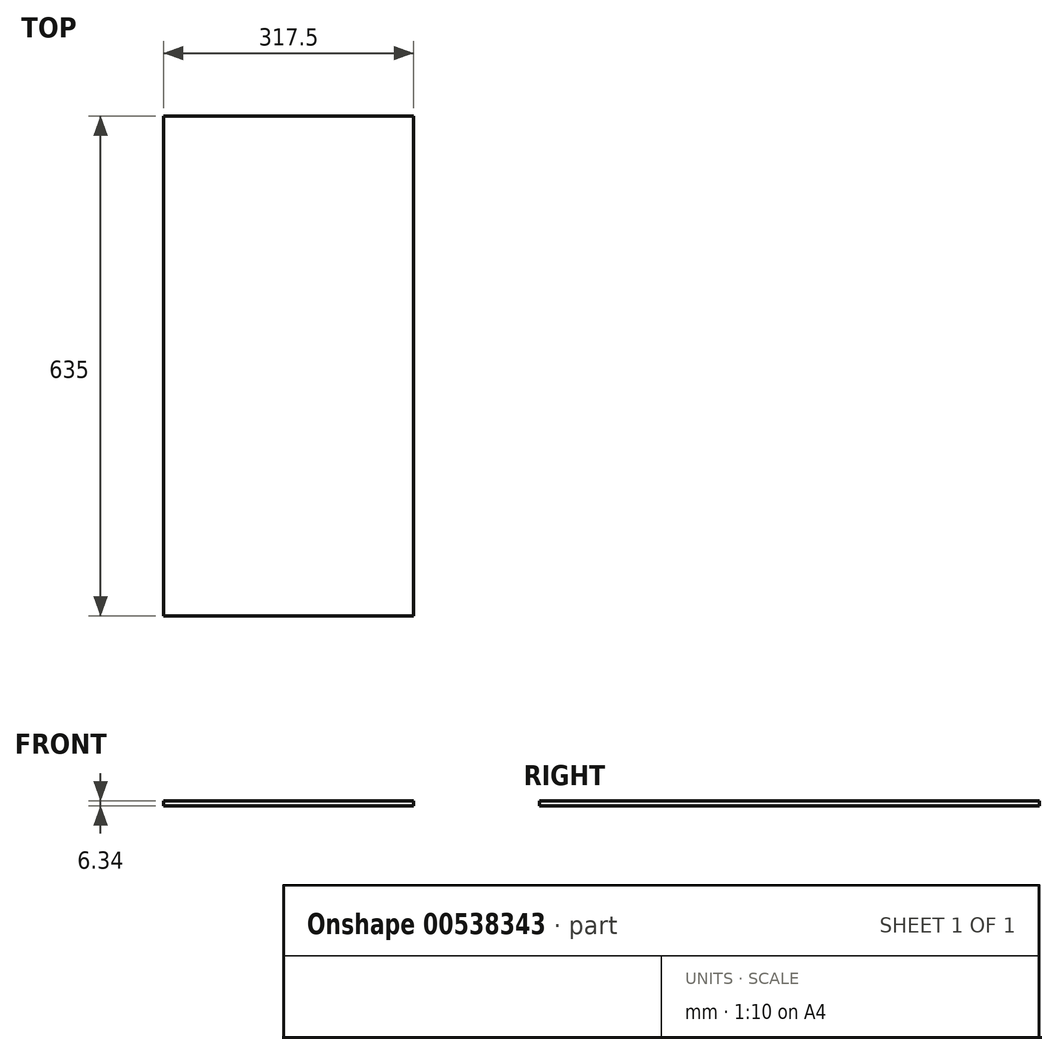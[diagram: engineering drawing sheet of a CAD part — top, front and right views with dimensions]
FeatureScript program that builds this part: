
annotation { "Feature Type Name" : "Feature", "Feature Type Description" : "" }
export const myFeature = defineFeature(function(context is Context, id is Id, definition is map)
    precondition{}
    {
        {
            var Q0;
            Q0=qCreatedBy(makeId("Top.planeOp"),FACE);
            var sketch = newSketch(context, id + "F0", { "sketchPlane" : qUnion([Q0])});
            skLineSegment(sketch, "E0.bottom", {"start": v(158.75, 317.5) * mm, "end": v(-158.75, 317.5) * mm});
            skLineSegment(sketch, "E0.top", {"start": v(158.75, -317.5) * mm, "end": v(-158.75, -317.5) * mm});
            skLineSegment(sketch, "E0.left", {"start": v(158.75, 317.5) * mm, "end": v(158.75, -317.5) * mm});
            skLineSegment(sketch, "E0.right", {"start": v(-158.75, 317.5) * mm, "end": v(-158.75, -317.5) * mm});
            skPoint(sketch, "E0.middle", {"position": v(0, 0) * mm});
            skSolve(sketch);
        }
        {
            var Q0;
            Q0=makeQuery(id+"F0.imprint","IMPRINT",FACE,{"disambiguationData":[TD([[makeQuery(id+"F0.imprint","IMPRINT",EDGE,{"derivedFrom":sQuery(id+"F0.wireOp",EDGE,"E0.bottom")}),1.0]])]});
            extrude(context, id + "F1", {"entities" : qUnion([Q0]), "endBound" : BoundingType.SYMMETRIC, "depth" : 6.35 * mm, "offsetDistance" : 25.4 * mm});
        }
    });
